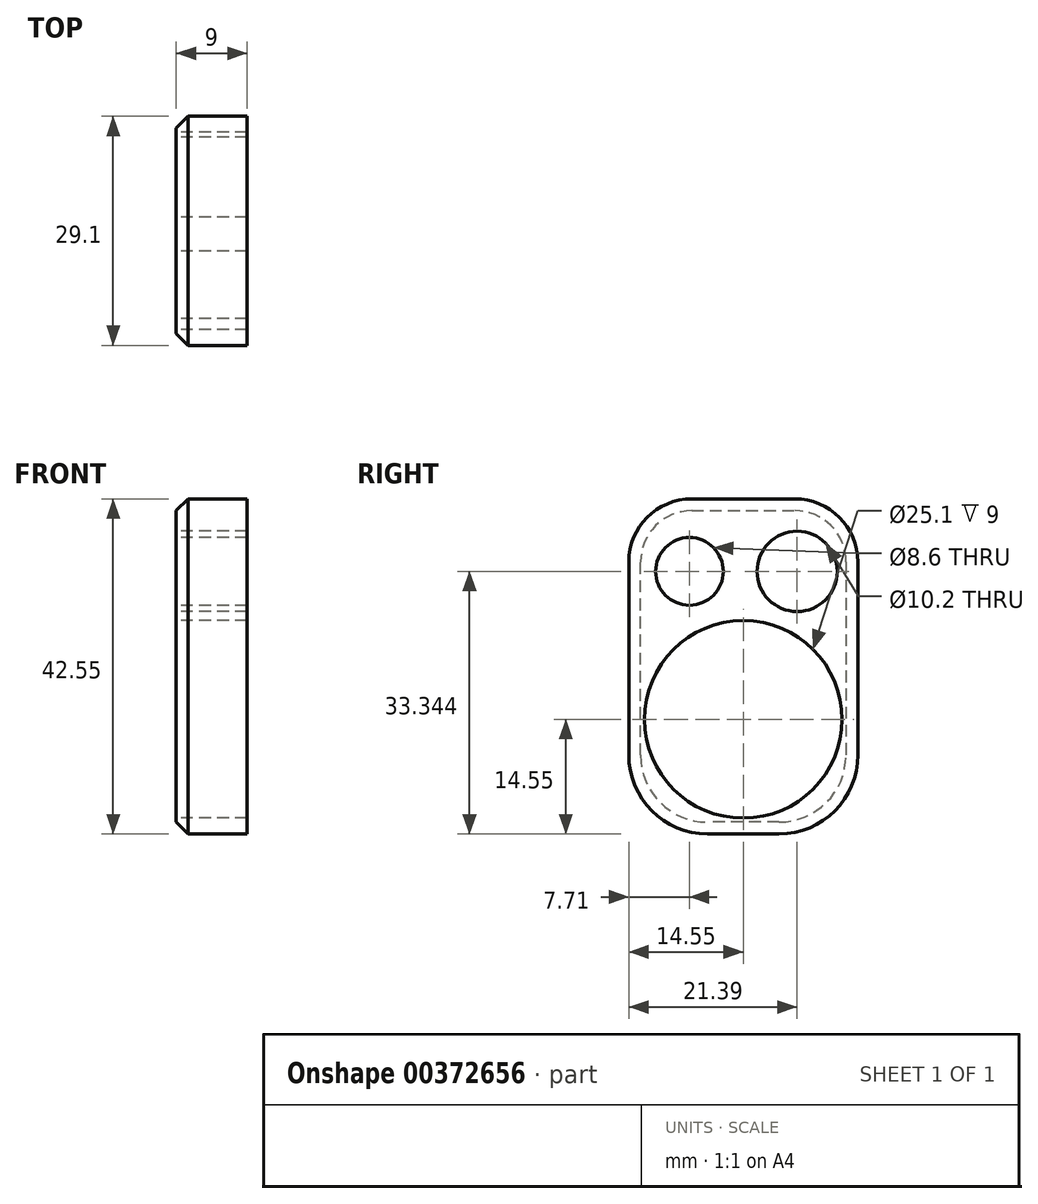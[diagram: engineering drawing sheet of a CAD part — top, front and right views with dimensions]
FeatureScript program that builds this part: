
annotation { "Feature Type Name" : "Feature", "Feature Type Description" : "" }
export const myFeature = defineFeature(function(context is Context, id is Id, definition is map)
    precondition{}
    {
        {
            var Q0;
            Q0=qCreatedBy(makeId("Right.planeOp"),FACE);
            var sketch = newSketch(context, id + "F0", { "sketchPlane" : qUnion([Q0])});
            skCircle(sketch, "E0", {"center": v(0, 0) * mm, "radius": 12.55 * mm});
            skCircle(sketch, "E1", {"center": v(-6.84, 18.8) * mm, "radius": 4.3 * mm});
            skCircle(sketch, "E2", {"center": v(6.84, 18.8) * mm, "radius": 5.1 * mm});
            skLineSegment(sketch, "E3", {"start": v(-6.84, 18.8) * mm, "end": v(0, 0) * mm, "construction": true});
            skLineSegment(sketch, "E4", {"start": v(6.84, 18.8) * mm, "end": v(0, 0) * mm, "construction": true});
            skCircle(sketch, "E5", {"center": v(-26, 0) * mm, "radius": 11 * mm});
            skLineSegment(sketch, "E6", {"start": v(-26, 0) * mm, "end": v(0, 0) * mm, "construction": true});
            skLineSegment(sketch, "E7", {"start": v(6.55, 28) * mm, "end": v(-6.55, 28) * mm});
            skLineSegment(sketch, "E8", {"start": v(14.55, 20) * mm, "end": v(14.55, -14.55) * mm});
            skLineSegment(sketch, "E9", {"start": v(-14.55, 20) * mm, "end": v(-14.55, -14.55) * mm});
            skLineSegment(sketch, "E10", {"start": v(-14.55, -14.55) * mm, "end": v(14.55, -14.55) * mm});
            skCircle(sketch, "E11", {"center": v(-6.84, 18.8) * mm, "radius": 2.5 * mm});
            skLineSegment(sketch, "E12", {"start": v(-6.84, 18.8) * mm, "end": v(-26, 0) * mm, "construction": true});
            skCircle(sketch, "E13", {"center": v(-6.84, 18.8) * mm, "radius": 3.25 * mm});
            skCircle(sketch, "E14", {"center": v(-26, 0) * mm, "radius": 13 * mm});
            skLineSegment(sketch, "E15", {"start": v(0, -14.55) * mm, "end": v(0, 0) * mm, "construction": true});
            skPoint(sketch, "E16.visualSharp", {"position": v(-14.55, 28) * mm});
            skArc(sketch, "E16.filletArc", {"start": v(-6.55, 28) * mm, "mid": v(-12.2, 25.66) * mm, "end": v(-14.55, 20) * mm});
            skPoint(sketch, "E17.visualSharp", {"position": v(14.55, 28) * mm});
            skArc(sketch, "E17.filletArc", {"start": v(14.55, 20) * mm, "mid": v(12.2, 25.66) * mm, "end": v(6.55, 28) * mm});
            skLineSegment(sketch, "E18", {"start": v(-18, -13) * mm, "end": v(-26, -13) * mm});
            skPoint(sketch, "E19.visualSharp", {"position": v(-13, -13) * mm});
            skArc(sketch, "E19.filletArc", {"start": v(-18, -13) * mm, "mid": v(-16.14, -12.64) * mm, "end": v(-14.55, -11.62) * mm});
            skLineSegment(sketch, "E20", {"start": v(-26, 13) * mm, "end": v(-14.55, 20) * mm});
            skSolve(sketch);
        }
        {
            var Q0;
            {var subQ6=sQuery(id+"F0.wireOp",EDGE,"E0");Q0=makeQuery(id+"F0.imprint","IMPRINT",FACE,{"disambiguationData":[TD([[makeQuery(id+"F0.imprint","IMPRINT",EDGE,{"derivedFrom":subQ6}),-1.0]])]});}
            var Q1;
            {var subQ0=sQuery(id+"F0.wireOp",EDGE,"E14");var subQ1=sQuery(id+"F0.wireOp",EDGE,"E9");var subQ2=makeQuery(id+"F0.imprint","INTERSECT",VERTEX,{"disambiguationData":[OD(0.0)],"derivedFrom":[subQ1,subQ0]});Q1=makeQuery(id+"F0.imprint","IMPRINT",FACE,{"disambiguationData":[TD([[makeQuery(id+"F0.imprint","IMPRINT",EDGE,{"disambiguationData":[TD([[subQ2,-1.0]])],"derivedFrom":subQ1}),1.0]])]});}
            extrude(context, id + "F1", {"entities" : qUnion([Q0, Q1]), "depth" : 9 * mm, "offsetDistance" : 25 * mm});
        }
        {
            var Q0;
            Q0=makeQuery(id+"F1.opExtrude","SWEPT_EDGE",EDGE,{"disambiguationData":[OSD([sQuery(id+"F0.wireOp",EDGE,"ezvYwHDF-qibp-4aTS-obrj-ytzPbMtdMMT9"),sQuery(id+"F0.wireOp",EDGE,"E8")])]});
            var Q1;
            Q1=makeQuery(id+"F1.opExtrude","SWEPT_EDGE",EDGE,{"disambiguationData":[OSD([sQuery(id+"F0.wireOp",EDGE,"E9"),sQuery(id+"F0.wireOp",EDGE,"E10")])]});
            var Q2;
            Q2=makeQuery(id+"F1.opExtrude","SWEPT_EDGE",EDGE,{"disambiguationData":[OSD([sQuery(id+"F0.wireOp",EDGE,"E8"),sQuery(id+"F0.wireOp",EDGE,"E10")])]});
            var Q3;
            Q3=makeQuery(id+"F150xzQlcN1fohN_1.opExtrude","SWEPT_EDGE",EDGE,{"disambiguationData":[OSD([sQuery(id+"F0.wireOp",EDGE,"E14"),sQuery(id+"F0.wireOp",EDGE,"H9HFL21Y-chsX-iVOF-3jS1-6DjapjbTuqdi")])]});
            fillet(context, id + "F2", {"entities" : qUnion([Q0, Q1, Q2, Q3]), "radius" : 10 * mm, "tangentPropagation" : true, "allowEdgeOverflow" : false});
        }
        {
            var Q0;
            Q0=makeQuery(id+"F1.opExtrude","CAP_FACE",FACE,{"disambiguationData":[OSD([sQuery(id+"F0.wireOp",EDGE,"E0"),sQuery(id+"F0.wireOp",EDGE,"E1"),sQuery(id+"F0.wireOp",EDGE,"E2"),sQuery(id+"F0.wireOp",EDGE,"E7"),sQuery(id+"F0.wireOp",EDGE,"E8"),sQuery(id+"F0.wireOp",EDGE,"E9"),sQuery(id+"F0.wireOp",EDGE,"E10"),sQuery(id+"F0.wireOp",EDGE,"E16.filletArc"),sQuery(id+"F0.wireOp",EDGE,"E17.filletArc")])],"isStart":true});
            var sketch = newSketch(context, id + "F3", { "sketchPlane" : qUnion([Q0])});
            skCircle(sketch, "E21", {"center": v(6.84, 18.8) * mm, "radius": 7.5 * mm});
            skCircle(sketch, "E22", {"center": v(6.84, 18.8) * mm, "radius": 5 * mm});
            skSolve(sketch);
        }
        {
            var Q0;
            Q0=makeQuery(id+"F1.opExtrude","CAP_EDGE",EDGE,{"disambiguationData":[OSD([sQuery(id+"F0.wireOp",EDGE,"E8")])],"isStart":true});
            chamfer(context, id + "F4", {"entities" : qUnion([Q0]), "width" : 1.5 * mm, "tangentPropagation" : true});
        }
    });
